# Revit family: HC_Heat Pump_MEPcontent_Itho Daalderop_WPV 90-180_NL-NL1
name_source: partatom
category: Mechanical Equipment
units: mm (PartAtom-declared; Revit-internal decimal feet)

## family parameters
Always vertical = Yes
Classification = None
Cut with Voids When Loaded = No
OmniClass Number = 23.75.10.21
OmniClass Title = Heat Pumps
Part Type = Normal
Room Calculation Point = No
Round Connector Dimension = Use Diameter
Shared = No
Work Plane-Based = No

## types (3) — shared parameters
Base Family Version = 23.10
Black = Color RGB 050-050-050
Content Supplier URL = www.MEPcontent.com
Cooling Power = 0 W
Custom = No
Depth = 500 mm  [stored 1.64042 ft]
Domestic Cold Water Diameter = 22 mm  [stored 0.0721785 ft]
Domestic Hot Water Diameter = 22 mm  [stored 0.0721785 ft]
EMCS Version = 5.0
ETIM Article Class = EC011794
Family Version = 23.10
GLN = 8712922000014
Heating Power = 0 W
Hertz = 50 Hz
Hydronic Return Diameter = 22 mm  [stored 0.0721785 ft]
Hydronic Supply Diameter = 22 mm  [stored 0.0721785 ft]
IFCExportAs = IfcPump
IFCExportType = NOTDEFINED
Light Grey = Color RAL 9006
MEPcontent Class = HEATPUMP
Manufacturer = Itho Daalderop
Manufacturer URL = https://www.ithodaalderop.nl
Phase = 1
Product Line = Itho Daalderop
Revit Version = 2021
Total Depth = 514.9 mm  [stored 1.6893 ft]
URL = https://mep.trimble.com
Voltage = 230 V
White = Color RAL 9003
Width = 500 mm  [stored 1.64042 ft]
zero-valued in all types: Back Clearance, Default Elevation

## per-type parameters (varying)
| type | Article Description | Description | GTIN | Height | Manufacturer Art. No. |
| WPV 3G 90L | WPV 3G 90L, warmtepomp voorraadvat 90L 3G | WPV 3G 90L, warmtepomp voorraadvat 90L 3G | 8713418048022 | 895 mm  [stored 2.93635 ft] | 03-00677 |
| WPV 3G 120L | WPV 3G 120L, warmtepomp voorraadvat 120L 3G | WPV 3G 120L, warmtepomp voorraadvat 120L 3G | 8713418048039 | 1069 mm | 03-00678 |
| WPV 3G 180L | WPV 3G 180L, warmtepomp voorraadvat 180L 3G | WPV 3G 180L, warmtepomp voorraadvat 180L 3G | 8713418048046 | 1561 mm | 03-00679 |

note: column(s) folded — value = type name in every type: Article Type, Model

type visibility flags (boolean, named after types; folded from table):
- WPV 3G 90L: Yes: (none)
- WPV 3G 120L: Yes: (none)
- WPV 3G 180L: Yes: WPV 3G 180L

note: [stored X ft] marks values corroborated as IEEE doubles in the binary element streams (Revit-internal decimal feet)

## geometry (parser evidence)
native form markers: Sweep x16
no freeform markers — native parametric forms only
